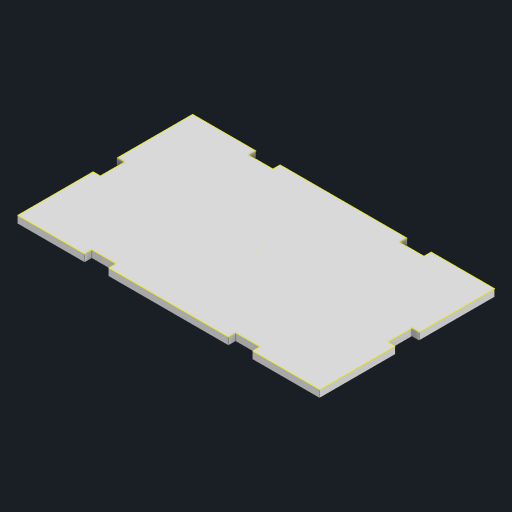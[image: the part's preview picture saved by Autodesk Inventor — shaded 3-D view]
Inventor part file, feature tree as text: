
AUTODESK INVENTOR PART (.ipt)
format: ipt  version: 2023 (Build 270158000, 158)  size: 134,144 bytes
history: native  units: mm
features: sketch x3, extrude x2, projected_geometry x1
ambient origin geometry x8: Origin, YZ Plane, XZ Plane, XY Plane, X Axis, Y Axis, Z Axis, Center Point
bodies: Solid1 (feature_tree)
feature tree (6):
  extrude  "Extrusion1"  Depth=73.0mm
  extrude  "Extrusion3"  Depth=10.0mm TaperAngle=0.0deg
  sketch  "Sketch4"
  sketch  "Sketch1"  dims[d0=126.0mm d1=73.0mm]
  sketch  "Sketch3"  dims[d2=3.0mm d3=0.0mm d6=10.0mm d7=0.0mm]
  projected_geometry  "Project Cut Edges2"
